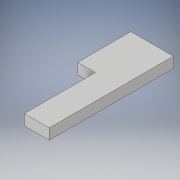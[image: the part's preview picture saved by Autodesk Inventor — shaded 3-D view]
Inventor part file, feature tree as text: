
AUTODESK INVENTOR PART (.ipt)
format: ipt  version: 2019 (Build 230136000, 136)  size: 121,856 bytes
history: native  units: in
note: dims shown in document units (in); Inventor stores cm internally (conversion verified against a paired STEP export)
features: extrude x2, sketch x2
ambient origin geometry x8: Origin, YZ Plane, XZ Plane, XY Plane, X Axis, Y Axis, Z Axis, Center Point
bodies: Solid1 (feature_tree)
feature tree (4):
  extrude  "Extrusion1"  Depth=0.5906in
  extrude  "Extrusion3"  Depth=0.0787in
  sketch  "Sketch1"  dims[d0=0.1969in d1=0.5906in]
  sketch  "Sketch3"  dims[d2=0.1181in d3=0.0in d7=0.0787in d8=0.2756in d9=0.0787in d10=0.0in d11=0.002in d12=0.002in d13=1.378in d14=0.2756in d18=0.1024in]
